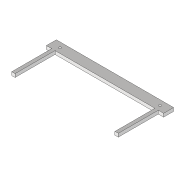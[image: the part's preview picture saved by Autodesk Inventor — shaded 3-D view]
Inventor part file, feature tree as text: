
AUTODESK INVENTOR PART (.ipt)
format: ipt  version: 2020 (Build 240168000, 168)  size: 97,280 bytes
history: native  units: mm
features: other x3, sketch x3
ambient origin geometry x8: Origin, YZ Plane, XZ Plane, XY Plane, X Axis, Y Axis, Z Axis, Center Point
bodies: Volumenkörper1 (feature_tree)
feature tree (6):
  other  "Gestell_Seite.ipt"
  other  "Volumenkörper1::Gestell_Seite.ipt"
  other  "Bezeichnung1"
  sketch  "Skizze1"  dims[d0=10.0mm]
  sketch  "Skizze2"
  sketch  "Skizze3"
